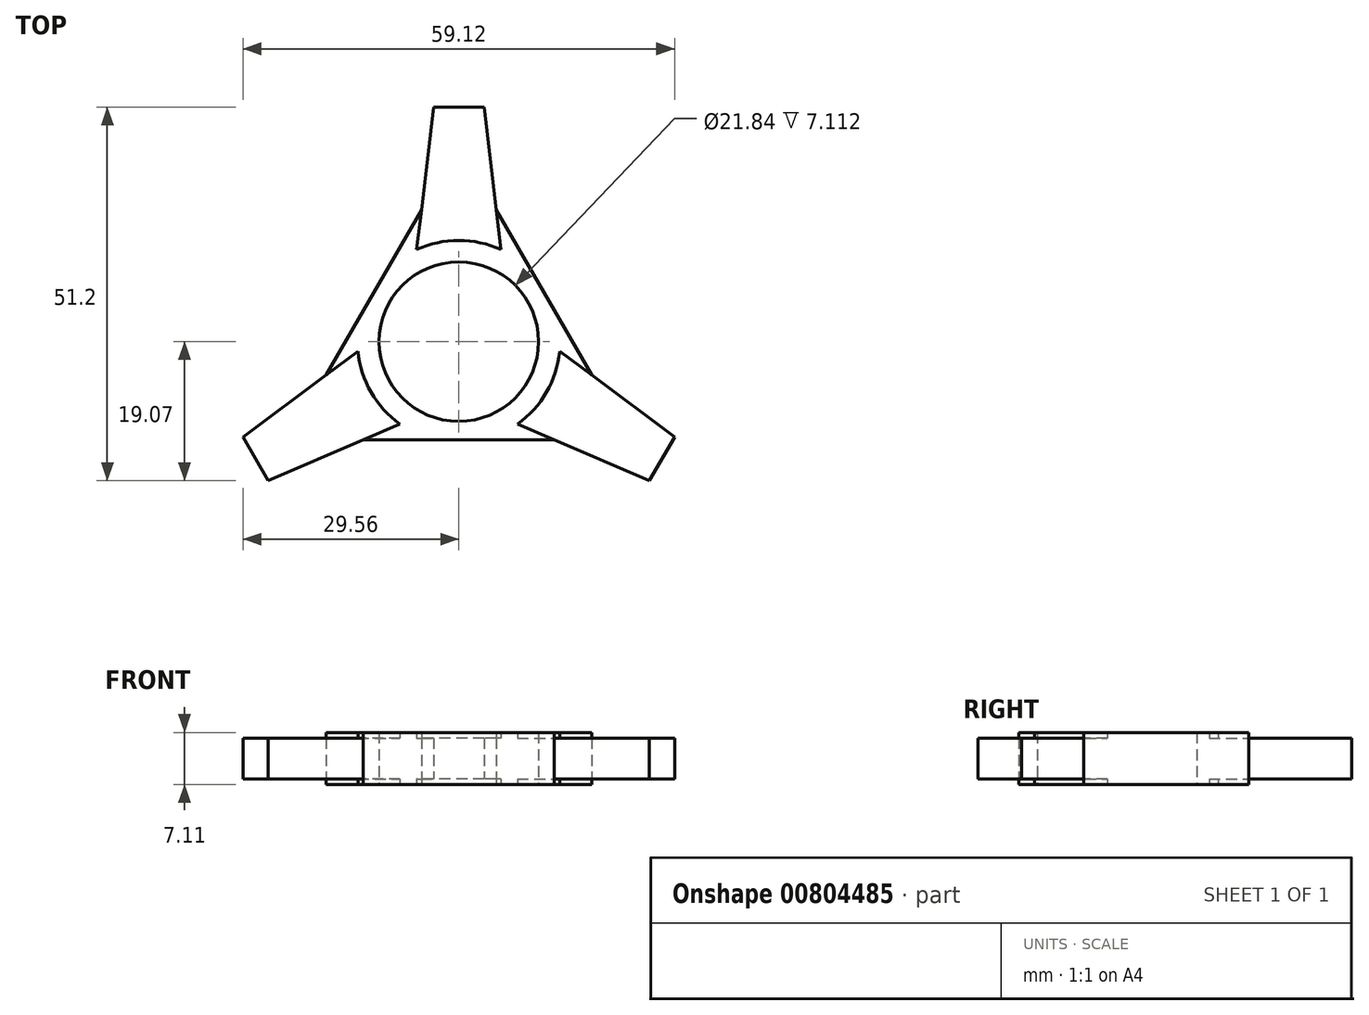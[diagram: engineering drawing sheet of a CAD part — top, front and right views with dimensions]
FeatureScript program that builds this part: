
annotation { "Feature Type Name" : "Feature", "Feature Type Description" : "" }
export const myFeature = defineFeature(function(context is Context, id is Id, definition is map)
    precondition{}
    {
        {
            var Q0;
            Q0=qCreatedBy(makeId("Top.planeOp"),FACE);
            var sketch = newSketch(context, id + "F0", { "sketchPlane" : qUnion([Q0])});
            skLineSegment(sketch, "E0", {"start": v(-5.92, 11.24) * mm, "end": v(-3.47, 32.13) * mm});
            skLineSegment(sketch, "E1.MirrorCS", {"start": v(5.92, 11.24) * mm, "end": v(3.47, 32.13) * mm});
            skLineSegment(sketch, "E2", {"start": v(3.47, 32.13) * mm, "end": v(-3.47, 32.13) * mm});
            skLineSegment(sketch, "E3.1.0", {"start": v(-6.77, -10.74) * mm, "end": v(-26.1, -19.07) * mm});
            skLineSegment(sketch, "E3.1.1", {"start": v(-12.7, -0.5) * mm, "end": v(-29.56, -13.06) * mm});
            skLineSegment(sketch, "E3.1.2", {"start": v(-29.56, -13.06) * mm, "end": v(-26.1, -19.07) * mm});
            skLineSegment(sketch, "E3.2.0", {"start": v(12.7, -0.5) * mm, "end": v(29.56, -13.06) * mm});
            skLineSegment(sketch, "E3.2.1", {"start": v(6.77, -10.74) * mm, "end": v(26.1, -19.07) * mm});
            skLineSegment(sketch, "E3.2.2", {"start": v(26.1, -19.07) * mm, "end": v(29.56, -13.06) * mm});
            skPoint(sketch, "E3.center", {"position": v(0, 0) * mm});
            skPoint(sketch, "E4.endSnap0", {"position": v(0, 32.13) * mm});
            skPoint(sketch, "E5", {"position": v(-5.12, 18.05) * mm});
            skPoint(sketch, "E6", {"position": v(5.12, 18.05) * mm});
            skPoint(sketch, "E7.1.0", {"position": v(-13.08, -13.46) * mm});
            skPoint(sketch, "E7.1.1", {"position": v(-18.2, -4.6) * mm});
            skPoint(sketch, "E7.2.0", {"position": v(18.2, -4.6) * mm});
            skPoint(sketch, "E7.2.1", {"position": v(13.08, -13.46) * mm});
            skCircle(sketch, "E8", {"center": v(0, 0) * mm, "radius": 10.92 * mm});
            skCircle(sketch, "E9", {"center": v(0, 0) * mm, "radius": 13.87 * mm});
            skPoint(sketch, "E10", {"position": v(-11.84, 7.22) * mm});
            skLineSegment(sketch, "E11", {"start": v(-13.08, -13.46) * mm, "end": v(13.08, -13.46) * mm});
            skLineSegment(sketch, "E12.1.0", {"start": v(18.2, -4.6) * mm, "end": v(5.12, 18.05) * mm});
            skLineSegment(sketch, "E12.2.0", {"start": v(-5.12, 18.05) * mm, "end": v(-18.2, -4.6) * mm});
            skSolve(sketch);
        }
        {
            var Q0;
            Q0=makeQuery(id+"F0.imprint","IMPRINT",FACE,{"disambiguationData":[TD([[makeQuery(id+"F0.imprint","IMPRINT",EDGE,{"derivedFrom":sQuery(id+"F0.wireOp",EDGE,"E8")}),-1.0]])]});
            extrude(context, id + "F1", {"entities" : qUnion([Q0]), "depth" : 7.11 * mm, "offsetDistance" : 25.4 * mm});
        }
        {
            var Q0;
            {var subQ0=sQuery(id+"F0.wireOp",EDGE,"E3.1.2");Q0=makeQuery(id+"F0.imprint","IMPRINT",FACE,{"disambiguationData":[TD([[makeQuery(id+"F0.imprint","IMPRINT",EDGE,{"derivedFrom":subQ0}),1.0]])]});}
            var Q1;
            {var subQ0=sQuery(id+"F0.wireOp",EDGE,"E2");Q1=makeQuery(id+"F0.imprint","IMPRINT",FACE,{"disambiguationData":[TD([[makeQuery(id+"F0.imprint","IMPRINT",EDGE,{"derivedFrom":subQ0}),1.0]])]});}
            var Q2;
            {var subQ0=sQuery(id+"F0.wireOp",EDGE,"E3.2.2");Q2=makeQuery(id+"F0.imprint","IMPRINT",FACE,{"disambiguationData":[TD([[makeQuery(id+"F0.imprint","IMPRINT",EDGE,{"derivedFrom":subQ0}),1.0]])]});}
            extrude(context, id + "F2", {"entities" : qUnion([Q0, Q1, Q2]), "operationType" : NewBodyOperationType.ADD, "depth" : 6.35 * mm, "offsetDistance" : 25.4 * mm});
        }
        {
            var Q0;
            {var subQ0=sQuery(id+"F0.wireOp",EDGE,"E3.2.2");Q0=makeQuery(id+"F0.imprint","IMPRINT",FACE,{"disambiguationData":[TD([[makeQuery(id+"F0.imprint","IMPRINT",EDGE,{"derivedFrom":subQ0}),1.0]])]});}
            var Q1;
            {var subQ0=sQuery(id+"F0.wireOp",EDGE,"E2");Q1=makeQuery(id+"F0.imprint","IMPRINT",FACE,{"disambiguationData":[TD([[makeQuery(id+"F0.imprint","IMPRINT",EDGE,{"derivedFrom":subQ0}),1.0]])]});}
            var Q2;
            {var subQ0=sQuery(id+"F0.wireOp",EDGE,"E3.1.2");Q2=makeQuery(id+"F0.imprint","IMPRINT",FACE,{"disambiguationData":[TD([[makeQuery(id+"F0.imprint","IMPRINT",EDGE,{"derivedFrom":subQ0}),1.0]])]});}
            extrude(context, id + "F3", {"entities" : qUnion([Q0, Q1, Q2]), "operationType" : NewBodyOperationType.REMOVE, "depth" : 0.76 * mm, "offsetDistance" : 25.4 * mm});
        }
        {
            var Q0;
            {var subQ0=sQuery(id+"F0.wireOp",EDGE,"a89b64c8-4102-4829-ae8c-ce16dc818629.2.0");var subQ1=sQuery(id+"F0.wireOp",EDGE,"E3.2.0");var subQ2=makeQuery(id+"F0.imprint","INTERSECT",VERTEX,{"derivedFrom":[subQ1,subQ0]});Q0=makeQuery(id+"F0.imprint","IMPRINT",FACE,{"disambiguationData":[TD([[makeQuery(id+"F0.imprint","IMPRINT",EDGE,{"disambiguationData":[TD([[subQ2,1.0]])],"derivedFrom":subQ1}),1.0]])]});}
            var Q1;
            {var subQ0=sQuery(id+"F0.wireOp",EDGE,"a89b64c8-4102-4829-ae8c-ce16dc818629.2.1");var subQ1=sQuery(id+"F0.wireOp",EDGE,"E1.MirrorCS");var subQ2=makeQuery(id+"F0.imprint","INTERSECT",VERTEX,{"derivedFrom":[subQ1,subQ0]});Q1=makeQuery(id+"F0.imprint","IMPRINT",FACE,{"disambiguationData":[TD([[makeQuery(id+"F0.imprint","IMPRINT",EDGE,{"disambiguationData":[TD([[subQ2,1.0]])],"derivedFrom":subQ1}),-1.0]])]});}
            var Q2;
            {var subQ0=sQuery(id+"F0.wireOp",EDGE,"qOnAdSvq-rPr2-1FKf-EDNZ-QJ1CGdZpWyNh");var subQ1=sQuery(id+"F0.wireOp",EDGE,"E0");var subQ2=makeQuery(id+"F0.imprint","INTERSECT",VERTEX,{"derivedFrom":[subQ1,subQ0]});Q2=makeQuery(id+"F0.imprint","IMPRINT",FACE,{"disambiguationData":[TD([[makeQuery(id+"F0.imprint","IMPRINT",EDGE,{"disambiguationData":[TD([[subQ2,1.0]])],"derivedFrom":subQ1}),1.0]])]});}
            var Q3;
            {var subQ0=sQuery(id+"F0.wireOp",EDGE,"E6tx37uq-zvGt-x9GZ-A5Bi-3dFuTgyA3a14");var subQ1=sQuery(id+"F0.wireOp",EDGE,"E3.1.1");var subQ2=makeQuery(id+"F0.imprint","INTERSECT",VERTEX,{"derivedFrom":[subQ1,subQ0]});Q3=makeQuery(id+"F0.imprint","IMPRINT",FACE,{"disambiguationData":[TD([[makeQuery(id+"F0.imprint","IMPRINT",EDGE,{"disambiguationData":[TD([[subQ2,1.0]])],"derivedFrom":subQ1}),-1.0]])]});}
            var Q4;
            {var subQ0=sQuery(id+"F0.wireOp",EDGE,"a89b64c8-4102-4829-ae8c-ce16dc818629.1.1");var subQ1=sQuery(id+"F0.wireOp",EDGE,"E3.2.1");var subQ2=makeQuery(id+"F0.imprint","INTERSECT",VERTEX,{"derivedFrom":[subQ1,subQ0]});Q4=makeQuery(id+"F0.imprint","IMPRINT",FACE,{"disambiguationData":[TD([[makeQuery(id+"F0.imprint","IMPRINT",EDGE,{"disambiguationData":[TD([[subQ2,1.0]])],"derivedFrom":subQ1}),-1.0]])]});}
            var Q5;
            {var subQ0=sQuery(id+"F0.wireOp",EDGE,"a89b64c8-4102-4829-ae8c-ce16dc818629.1.0");var subQ1=sQuery(id+"F0.wireOp",EDGE,"E3.1.0");var subQ2=makeQuery(id+"F0.imprint","INTERSECT",VERTEX,{"derivedFrom":[subQ1,subQ0]});Q5=makeQuery(id+"F0.imprint","IMPRINT",FACE,{"disambiguationData":[TD([[makeQuery(id+"F0.imprint","IMPRINT",EDGE,{"disambiguationData":[TD([[subQ2,1.0]])],"derivedFrom":subQ1}),1.0]])]});}
            extrude(context, id + "F4", {"entities" : qUnion([Q0, Q1, Q2, Q3, Q4, Q5]), "operationType" : NewBodyOperationType.ADD, "depth" : 7.11 * mm, "offsetDistance" : 25.4 * mm});
        }
    });
